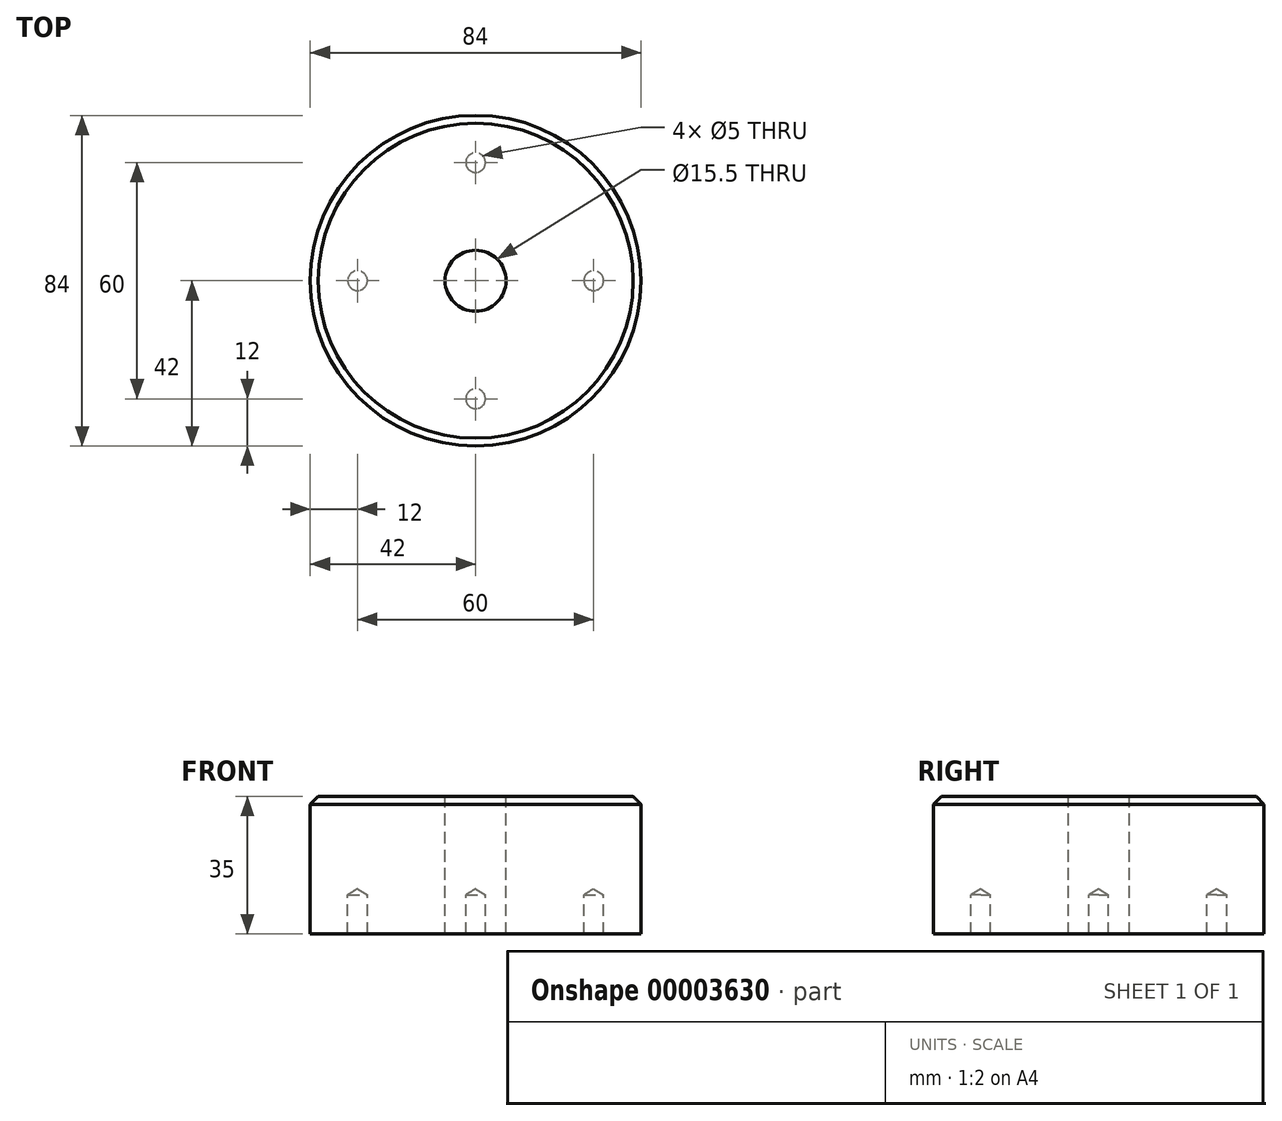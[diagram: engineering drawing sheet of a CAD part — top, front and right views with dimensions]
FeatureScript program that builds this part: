
annotation { "Feature Type Name" : "Feature", "Feature Type Description" : "" }
export const myFeature = defineFeature(function(context is Context, id is Id, definition is map)
    precondition{}
    {
        {
            var Q0;
            Q0=qCreatedBy(makeId("Top.planeOp"),FACE);
            var sketch = newSketch(context, id + "F0", { "sketchPlane" : qUnion([Q0])});
            skCircle(sketch, "E0", {"center": v(0, 0) * mm, "radius": 42 * mm});
            skSolve(sketch);
        }
        {
            var Q0;
            Q0=makeQuery(id+"F0.imprint","IMPRINT",FACE,{"disambiguationData":[TD([[makeQuery(id+"F0.imprint","IMPRINT",EDGE,{"derivedFrom":sQuery(id+"F0.wireOp",EDGE,"E0")}),1.0]])]});
            extrude(context, id + "F1", {"entities" : qUnion([Q0]), "depth" : 35 * mm});
        }
        {
            var Q0;
            Q0=makeQuery(id+"F1.opExtrude","CAP_EDGE",EDGE,{"disambiguationData":[OSD([sQuery(id+"F0.wireOp",EDGE,"E0")])],"isStart":false});
            chamfer(context, id + "F2", {"entities" : qUnion([Q0]), "width" : 2 * mm, "tangentPropagation" : true});
        }
        {
            var Q0;
            Q0=qCreatedBy(makeId("Top.planeOp"),FACE);
            var sketch = newSketch(context, id + "F3", { "sketchPlane" : qUnion([Q0])});
            skCircle(sketch, "E1", {"center": v(0, 0) * mm, "radius": 30 * mm, "construction": true});
            skPoint(sketch, "E2", {"position": v(0, -30) * mm});
            skPoint(sketch, "E3", {"position": v(0, 30) * mm});
            skPoint(sketch, "E4", {"position": v(30, 0) * mm});
            skPoint(sketch, "E5", {"position": v(-30, 0) * mm});
            skSolve(sketch);
        }
        {
            var Q0;
            Q0=sQuery(id+"F3.wireOp",VERTEX,"E1.center");
            var Q1;
            Q1=makeQuery(id+"F1.opExtrude","SWEPT_BODY",BODY,{"disambiguationData":[OSD([sQuery(id+"F0.wireOp",EDGE,"E0")])]});
            hole(context, id + "F4", {"style" : HoleStyle.SIMPLE, "endStyle" : HoleEndStyle.THROUGH, "oppositeDirection" : true, "standardTappedOrClearance" : lookupTablePath({ "standard" : "ISO", "fit" : "Normal", "size" : "M14", "type" : "Clearance" }), "standardBlindInLast" : lookupTablePath({ "fit" : "Standard", "standard" : "ISO", "size" : "M14", "type" : "Clearance" }), "holeDiameter" : 15.5 * mm, "tappedDepth" : 7 * mm, "tapClearance" : 3, "locations" : qUnion([Q0]), "scope" : qUnion([Q1]), "startStyle" : HoleStartStyle.SKETCH});
        }
        {
            var Q0;
            Q0=sQuery(id+"F3.wireOp",VERTEX,"E2");
            var Q1;
            Q1=sQuery(id+"F3.wireOp",VERTEX,"E4");
            var Q2;
            Q2=sQuery(id+"F3.wireOp",VERTEX,"E3");
            var Q3;
            Q3=sQuery(id+"F3.wireOp",VERTEX,"E5");
            var Q4;
            Q4=makeQuery(id+"F1.opExtrude","SWEPT_BODY",BODY,{"disambiguationData":[OSD([sQuery(id+"F0.wireOp",EDGE,"E0")])]});
            hole(context, id + "F5", {"style" : HoleStyle.SIMPLE, "endStyle" : HoleEndStyle.BLIND, "oppositeDirection" : true, "standardTappedOrClearance" : lookupTablePath({ "standard" : "ISO", "engagement" : "75%", "pitch" : "1 mm", "size" : "M6", "type" : "Tapped" }), "standardBlindInLast" : lookupTablePath({ "standard" : "ISO", "engagement" : "75%", "pitch" : "1 mm", "size" : "M6", "type" : "Tapped" }), "holeDiameter" : 5 * mm, "showTappedDepth" : true, "holeDepth" : 10 * mm, "tappedDepth" : 7 * mm, "tapClearance" : 3, "locations" : qUnion([Q0, Q1, Q2, Q3]), "scope" : qUnion([Q4]), "majorDiameter" : 6 * mm, "startStyle" : HoleStartStyle.SKETCH});
        }
    });
